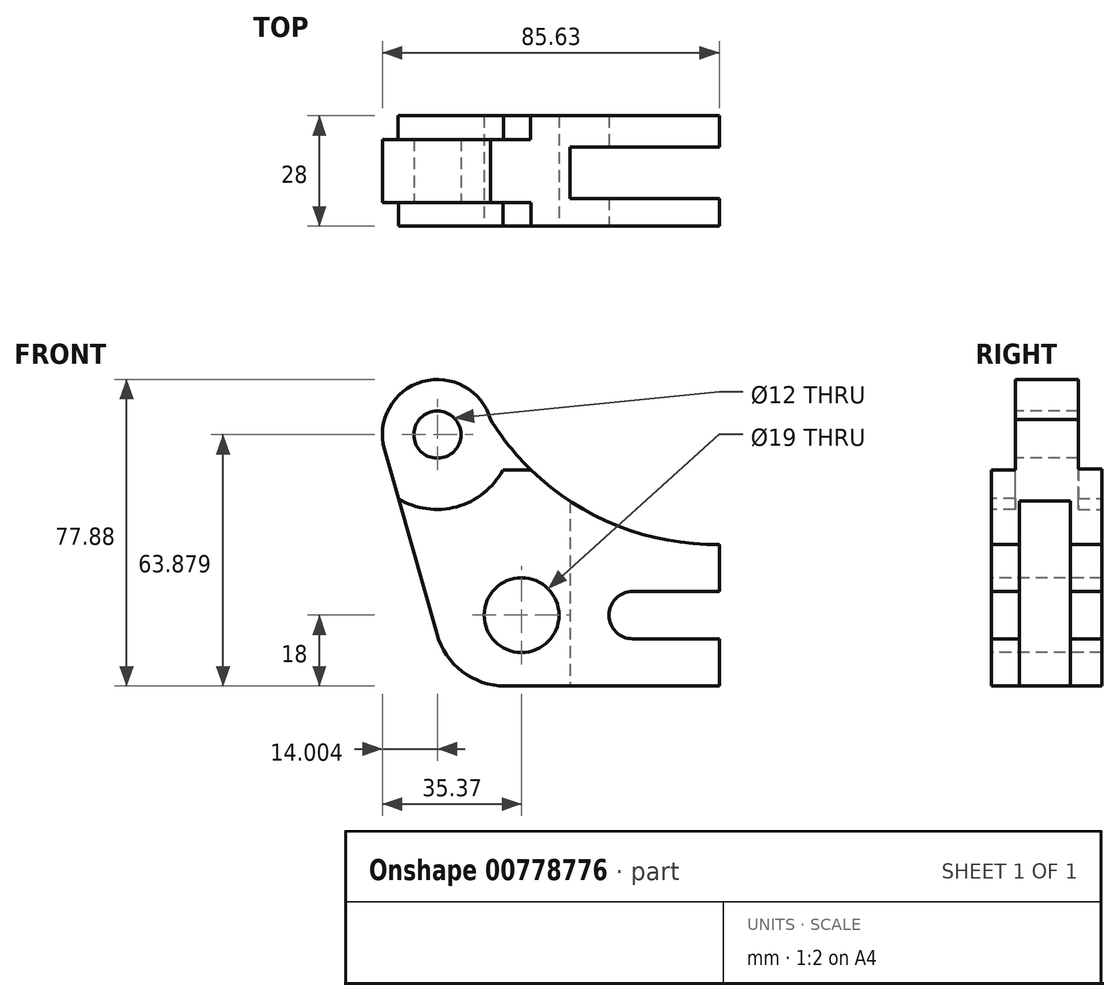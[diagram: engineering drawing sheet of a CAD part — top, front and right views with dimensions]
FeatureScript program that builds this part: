
annotation { "Feature Type Name" : "Feature", "Feature Type Description" : "" }
export const myFeature = defineFeature(function(context is Context, id is Id, definition is map)
    precondition{}
    {
        {
            var Q0;
            Q0=qCreatedBy(makeId("Front.planeOp"),FACE);
            var sketch = newSketch(context, id + "F0", { "sketchPlane" : qUnion([Q0])});
            skLineSegment(sketch, "E0", {"start": v(50.26, 0) * mm, "end": v(-4.16, 0) * mm});
            skLineSegment(sketch, "E1", {"start": v(50.26, 0) * mm, "end": v(50.26, 36) * mm});
            skArc(sketch, "E2.filletArc", {"start": v(-21.52, 13.23) * mm, "mid": v(-15.07, 3.69) * mm, "end": v(-4.16, 0) * mm});
            skCircle(sketch, "E3", {"center": v(-4.16, 18) * mm, "radius": 9.5 * mm});
            skLineSegment(sketch, "E4", {"start": v(50.26, 36) * mm, "end": v(50.26, 36) * mm});
            skArc(sketch, "E5.filletArc", {"start": v(-7.9, 67.7) * mm, "mid": v(16.99, 44.16) * mm, "end": v(50.26, 36) * mm});
            skCircle(sketch, "E6", {"center": v(-21.37, 63.88) * mm, "radius": 14 * mm});
            skLineSegment(sketch, "E7", {"start": v(-21.43, 12.92) * mm, "end": v(-34.83, 60.05) * mm});
            skCircle(sketch, "E8", {"center": v(-21.37, 63.88) * mm, "radius": 6 * mm});
            skSolve(sketch);
        }
        {
            var Q0;
            {var subQ1=sQuery(id+"F0.wireOp",EDGE,"E0");Q0=makeQuery(id+"F0.imprint","IMPRINT",FACE,{"disambiguationData":[TD([[makeQuery(id+"F0.imprint","IMPRINT",EDGE,{"derivedFrom":subQ1}),-1.0]])]});}
            var Q1;
            Q1=makeQuery(id+"F0.imprint","IMPRINT",FACE,{"disambiguationData":[TD([[makeQuery(id+"F0.imprint","IMPRINT",EDGE,{"derivedFrom":sQuery(id+"F0.wireOp",EDGE,"E8")}),1.0]])]});
            var Q2;
            Q2=makeQuery(id+"F0.imprint","IMPRINT",FACE,{"disambiguationData":[TD([[makeQuery(id+"F0.imprint","IMPRINT",EDGE,{"derivedFrom":sQuery(id+"F0.wireOp",EDGE,"E8")}),-1.0]])]});
            var Q3;
            Q3=makeQuery(id+"F0.imprint","IMPRINT",FACE,{"disambiguationData":[TD([[makeQuery(id+"F0.imprint","IMPRINT",EDGE,{"derivedFrom":sQuery(id+"F0.wireOp",EDGE,"E3")}),1.0]])]});
            var Q4;
            {var subQ0=sQuery(id+"F0.wireOp",EDGE,"E7");var subQ1=sQuery(id+"F0.wireOp",EDGE,"E2.filletArc");var subQ2=makeQuery(id+"F0.imprint","INTERSECT",VERTEX,{"disambiguationData":[OD(0.0)],"derivedFrom":[subQ1,subQ0]});Q4=makeQuery(id+"F0.imprint","IMPRINT",FACE,{"disambiguationData":[TD([[makeQuery(id+"F0.imprint","IMPRINT",EDGE,{"disambiguationData":[TD([[subQ2,-1.0]])],"derivedFrom":subQ1}),1.0]])]});}
            extrude(context, id + "F1", {"entities" : qUnion([Q0, Q1, Q2, Q3, Q4]), "depth" : 28 * mm, "offsetDistance" : 25 * mm});
        }
        {
            var Q0;
            Q0=makeQuery(id+"F1.opExtrude","CAP_FACE",FACE,{"disambiguationData":[OSD([sQuery(id+"F0.wireOp",EDGE,"E0"),sQuery(id+"F0.wireOp",EDGE,"E2.filletArc"),sQuery(id+"F0.wireOp",EDGE,"E1"),sQuery(id+"F0.wireOp",EDGE,"E5.filletArc"),sQuery(id+"F0.wireOp",EDGE,"E6"),sQuery(id+"F0.wireOp",EDGE,"E7")])],"isStart":false});
            var sketch = newSketch(context, id + "F2", { "sketchPlane" : qUnion([Q0])});
            skLineSegment(sketch, "E9", {"start": v(0, 0) * mm, "end": v(0, 18) * mm});
            skLineSegment(sketch, "E10", {"start": v(0, 18) * mm, "end": v(50.26, 18) * mm});
            skSolve(sketch);
        }
        {
            var Q0;
            Q0=sQuery(id+"F2.wireOp",VERTEX,"E9.end");
            var Q1;
            Q1=makeQuery(id+"F1.opExtrude","SWEPT_BODY",BODY,{"disambiguationData":[OSD([sQuery(id+"F0.wireOp",EDGE,"E0"),sQuery(id+"F0.wireOp",EDGE,"E2.filletArc"),sQuery(id+"F0.wireOp",EDGE,"E1"),sQuery(id+"F0.wireOp",EDGE,"E5.filletArc"),sQuery(id+"F0.wireOp",EDGE,"E6"),sQuery(id+"F0.wireOp",EDGE,"E7")])]});
            hole(context, id + "F3", {"style" : HoleStyle.SIMPLE, "endStyle" : HoleEndStyle.THROUGH, "holeDiameter" : 19 * mm, "majorDiameter" : 5 * mm, "isTappedThrough" : true, "tappedDepth" : 12 * mm, "tapClearance" : 3, "locations" : qUnion([Q0]), "scope" : qUnion([Q1])});
        }
        {
            var Q0;
            Q0=makeQuery(id+"F1.opExtrude","CAP_FACE",FACE,{"disambiguationData":[OSD([sQuery(id+"F0.wireOp",EDGE,"E0"),sQuery(id+"F0.wireOp",EDGE,"E2.filletArc"),sQuery(id+"F0.wireOp",EDGE,"E1"),sQuery(id+"F0.wireOp",EDGE,"E5.filletArc"),sQuery(id+"F0.wireOp",EDGE,"E6"),sQuery(id+"F0.wireOp",EDGE,"E7")])],"isStart":false});
            var sketch = newSketch(context, id + "F4", { "sketchPlane" : qUnion([Q0])});
            skLineSegment(sketch, "E11", {"start": v(0, 18) * mm, "end": v(-21.37, 63.88) * mm});
            skSolve(sketch);
        }
        {
            var Q0;
            Q0=sQuery(id+"F4.wireOp",VERTEX,"E11.end");
            var Q1;
            Q1=makeQuery(id+"F1.opExtrude","SWEPT_BODY",BODY,{"disambiguationData":[OSD([sQuery(id+"F0.wireOp",EDGE,"E0"),sQuery(id+"F0.wireOp",EDGE,"E2.filletArc"),sQuery(id+"F0.wireOp",EDGE,"E1"),sQuery(id+"F0.wireOp",EDGE,"E5.filletArc"),sQuery(id+"F0.wireOp",EDGE,"E6"),sQuery(id+"F0.wireOp",EDGE,"E7")])]});
            hole(context, id + "F5", {"style" : HoleStyle.SIMPLE, "endStyle" : HoleEndStyle.THROUGH, "holeDiameter" : 12 * mm, "majorDiameter" : 5 * mm, "isTappedThrough" : true, "tappedDepth" : 12 * mm, "tapClearance" : 3, "locations" : qUnion([Q0]), "scope" : qUnion([Q1])});
        }
        {
            var Q0;
            Q0=makeQuery(id+"F1.opExtrude","CAP_FACE",FACE,{"disambiguationData":[OSD([sQuery(id+"F0.wireOp",EDGE,"E0"),sQuery(id+"F0.wireOp",EDGE,"E2.filletArc"),sQuery(id+"F0.wireOp",EDGE,"E1"),sQuery(id+"F0.wireOp",EDGE,"E5.filletArc"),sQuery(id+"F0.wireOp",EDGE,"E6"),sQuery(id+"F0.wireOp",EDGE,"E7")])],"isStart":false});
            var sketch = newSketch(context, id + "F6", { "sketchPlane" : qUnion([Q0])});
            skArc(sketch, "E12", {"start": v(-31.3, 47.6) * mm, "mid": v(-16.46, 45.55) * mm, "end": v(-4.74, 54.87) * mm});
            skLineSegment(sketch, "E13", {"start": v(2.43, 54.87) * mm, "end": v(-4.74, 54.87) * mm});
            skPoint(sketch, "E14.orphan", {"position": v(-21.48, 54.87) * mm});
            skLineSegment(sketch, "E15", {"start": v(-31.3, 47.6) * mm, "end": v(-34.83, 60.05) * mm});
            skSolve(sketch);
        }
        {
            var Q0;
            Q0=makeQuery(id+"F6.imprint","IMPRINT",FACE,{"disambiguationData":[TD([[makeQuery(id+"F6.imprint","IMPRINT",EDGE,{"derivedFrom":sQuery(id+"F6.wireOp",EDGE,"E12")}),1.0]])]});
            extrude(context, id + "F7", {"entities" : qUnion([Q0]), "operationType" : NewBodyOperationType.ADD, "oppositeDirection" : true, "depth" : 6 * mm, "offsetDistance" : 25 * mm});
        }
        {
            var Q0;
            Q0=makeQuery(id+"F6.imprint","IMPRINT",FACE,{"disambiguationData":[TD([[makeQuery(id+"F6.imprint","IMPRINT",EDGE,{"derivedFrom":sQuery(id+"F6.wireOp",EDGE,"E12")}),1.0]])]});
            extrude(context, id + "F8", {"entities" : qUnion([Q0]), "operationType" : NewBodyOperationType.ADD, "oppositeDirection" : true, "depth" : 6 * mm, "offsetDistance" : 25 * mm});
        }
        {
            var Q0;
            Q0=makeQuery(id+"F6.imprint","IMPRINT",FACE,{"disambiguationData":[TD([[makeQuery(id+"F6.imprint","IMPRINT",EDGE,{"derivedFrom":sQuery(id+"F6.wireOp",EDGE,"E12")}),1.0]])]});
            extrude(context, id + "F9", {"entities" : qUnion([Q0]), "operationType" : NewBodyOperationType.ADD, "oppositeDirection" : true, "depth" : 6 * mm, "offsetDistance" : 25 * mm});
        }
        {
            var Q0;
            Q0=makeQuery(id+"F6.imprint","IMPRINT",FACE,{"disambiguationData":[TD([[makeQuery(id+"F6.imprint","IMPRINT",EDGE,{"derivedFrom":sQuery(id+"F6.wireOp",EDGE,"E12")}),1.0]])]});
            extrude(context, id + "F10", {"entities" : qUnion([Q0]), "operationType" : NewBodyOperationType.REMOVE, "oppositeDirection" : true, "depth" : 6 * mm, "offsetDistance" : 25 * mm});
        }
        {
            var Q0;
            Q0=makeQuery(id+"F1.opExtrude","CAP_FACE",FACE,{"disambiguationData":[OSD([sQuery(id+"F0.wireOp",EDGE,"E0"),sQuery(id+"F0.wireOp",EDGE,"E2.filletArc"),sQuery(id+"F0.wireOp",EDGE,"E1"),sQuery(id+"F0.wireOp",EDGE,"E5.filletArc"),sQuery(id+"F0.wireOp",EDGE,"E6"),sQuery(id+"F0.wireOp",EDGE,"E7")])],"isStart":true});
            var sketch = newSketch(context, id + "F11", { "sketchPlane" : qUnion([Q0])});
            skArc(sketch, "E16", {"start": v(4.53, 55.08) * mm, "mid": v(16.32, 45.56) * mm, "end": v(31.32, 47.7) * mm});
            skLineSegment(sketch, "E17", {"start": v(4.53, 55.08) * mm, "end": v(-2.22, 55.08) * mm});
            skSolve(sketch);
        }
        {
            var Q0;
            {var subQ5=sQuery(id+"F11.wireOp",EDGE,"E16");Q0=makeQuery(id+"F11.imprint","IMPRINT",FACE,{"disambiguationData":[TD([[makeQuery(id+"F11.imprint","IMPRINT",EDGE,{"derivedFrom":subQ5}),1.0]])]});}
            extrude(context, id + "F12", {"entities" : qUnion([Q0]), "operationType" : NewBodyOperationType.REMOVE, "oppositeDirection" : true, "depth" : 6 * mm, "offsetDistance" : 25 * mm});
        }
        {
            var Q0;
            Q0=makeQuery(id+"F1.opExtrude","SWEPT_FACE",FACE,{"disambiguationData":[OSD([sQuery(id+"F0.wireOp",EDGE,"E1")])]});
            var sketch = newSketch(context, id + "F13", { "sketchPlane" : qUnion([Q0])});
            skLineSegment(sketch, "E18", {"start": v(-8, 36) * mm, "end": v(-8, 0) * mm});
            skLineSegment(sketch, "E19.bottom", {"start": v(-8, 0) * mm, "end": v(-21, 0) * mm});
            skLineSegment(sketch, "E19.left", {"start": v(-8, 0) * mm, "end": v(-8, 36) * mm});
            skLineSegment(sketch, "E19.right", {"start": v(-21, 0) * mm, "end": v(-21, 36) * mm});
            skLineSegment(sketch, "E20.bottom", {"start": v(-21, 0) * mm, "end": v(-8, 0) * mm});
            skLineSegment(sketch, "E20.top", {"start": v(-21, 0) * mm, "end": v(-8, 0) * mm});
            skLineSegment(sketch, "E20.left", {"start": v(-21, 0) * mm, "end": v(-21, 0) * mm});
            skLineSegment(sketch, "E20.right", {"start": v(-8, 0) * mm, "end": v(-8, 0) * mm});
            skLineSegment(sketch, "E21.left", {"start": v(-8, 52.06) * mm, "end": v(-8, 0) * mm});
            skLineSegment(sketch, "E21.right", {"start": v(-21, 52.06) * mm, "end": v(-21, 0) * mm});
            skLineSegment(sketch, "E22.left", {"start": v(-8, 52.06) * mm, "end": v(-8, 52.06) * mm});
            skLineSegment(sketch, "E22.right", {"start": v(-21, 52.06) * mm, "end": v(-21, 52.06) * mm});
            skLineSegment(sketch, "E23.bottom", {"start": v(-8, 58.4) * mm, "end": v(-21, 58.4) * mm});
            skLineSegment(sketch, "E23.left", {"start": v(-8, 58.4) * mm, "end": v(-8, 52.06) * mm});
            skLineSegment(sketch, "E23.right", {"start": v(-21, 58.4) * mm, "end": v(-21, 52.06) * mm});
            skSolve(sketch);
        }
        {
            var Q0;
            Q0=makeQuery(id+"F13.imprint","IMPRINT",FACE,{"disambiguationData":[TD([[makeQuery(id+"F13.imprint","IMPRINT",EDGE,{"derivedFrom":sQuery(id+"F13.wireOp",EDGE,"E19.bottom")}),1.0]])]});
            extrude(context, id + "F14", {"entities" : qUnion([Q0]), "operationType" : NewBodyOperationType.REMOVE, "depth" : 38 * mm, "offsetDistance" : 25 * mm});
        }
        {
            var Q0;
            Q0=makeQuery(id+"F13.imprint","IMPRINT",FACE,{"disambiguationData":[TD([[makeQuery(id+"F13.imprint","IMPRINT",EDGE,{"derivedFrom":sQuery(id+"F13.wireOp",EDGE,"E23.bottom")}),1.0]])]});
            var Q1;
            {var subQ0=sQuery(id+"F13.wireOp",EDGE,"E19.bottom");Q1=makeQuery(id+"F13.imprint","IMPRINT",FACE,{"disambiguationData":[TD([[makeQuery(id+"F13.imprint","IMPRINT",EDGE,{"derivedFrom":subQ0}),1.0]])]});}
            extrude(context, id + "F15", {"entities" : qUnion([Q0, Q1]), "operationType" : NewBodyOperationType.REMOVE, "oppositeDirection" : true, "depth" : 38 * mm, "offsetDistance" : 25 * mm});
        }
        {
            var Q0;
            {var subQ2=sQuery(id+"F6.wireOp",EDGE,"E12");Q0=makeQuery(id+"F6.imprint","IMPRINT",FACE,{"disambiguationData":[TD([[makeQuery(id+"F6.imprint","IMPRINT",EDGE,{"derivedFrom":subQ2}),-1.0]])]});}
            var sketch = newSketch(context, id + "F16", { "sketchPlane" : qUnion([Q0])});
            skLineSegment(sketch, "E24", {"start": v(50.27, 12) * mm, "end": v(50.27, 24) * mm});
            skLineSegment(sketch, "E25", {"start": v(50.27, 12) * mm, "end": v(28.23, 12) * mm});
            skLineSegment(sketch, "E26", {"start": v(28.23, 24) * mm, "end": v(50.27, 24) * mm});
            skArc(sketch, "E27", {"start": v(28.23, 24) * mm, "mid": v(22.23, 18) * mm, "end": v(28.23, 12) * mm});
            skSolve(sketch);
        }
        {
            var Q0;
            Q0 = qSketchRegion(id + "F16", true);
            extrude(context, id + "F17", {"entities" : qUnion([Q0]), "operationType" : NewBodyOperationType.REMOVE, "oppositeDirection" : true, "depth" : 28 * mm, "offsetDistance" : 25 * mm});
        }
    });
